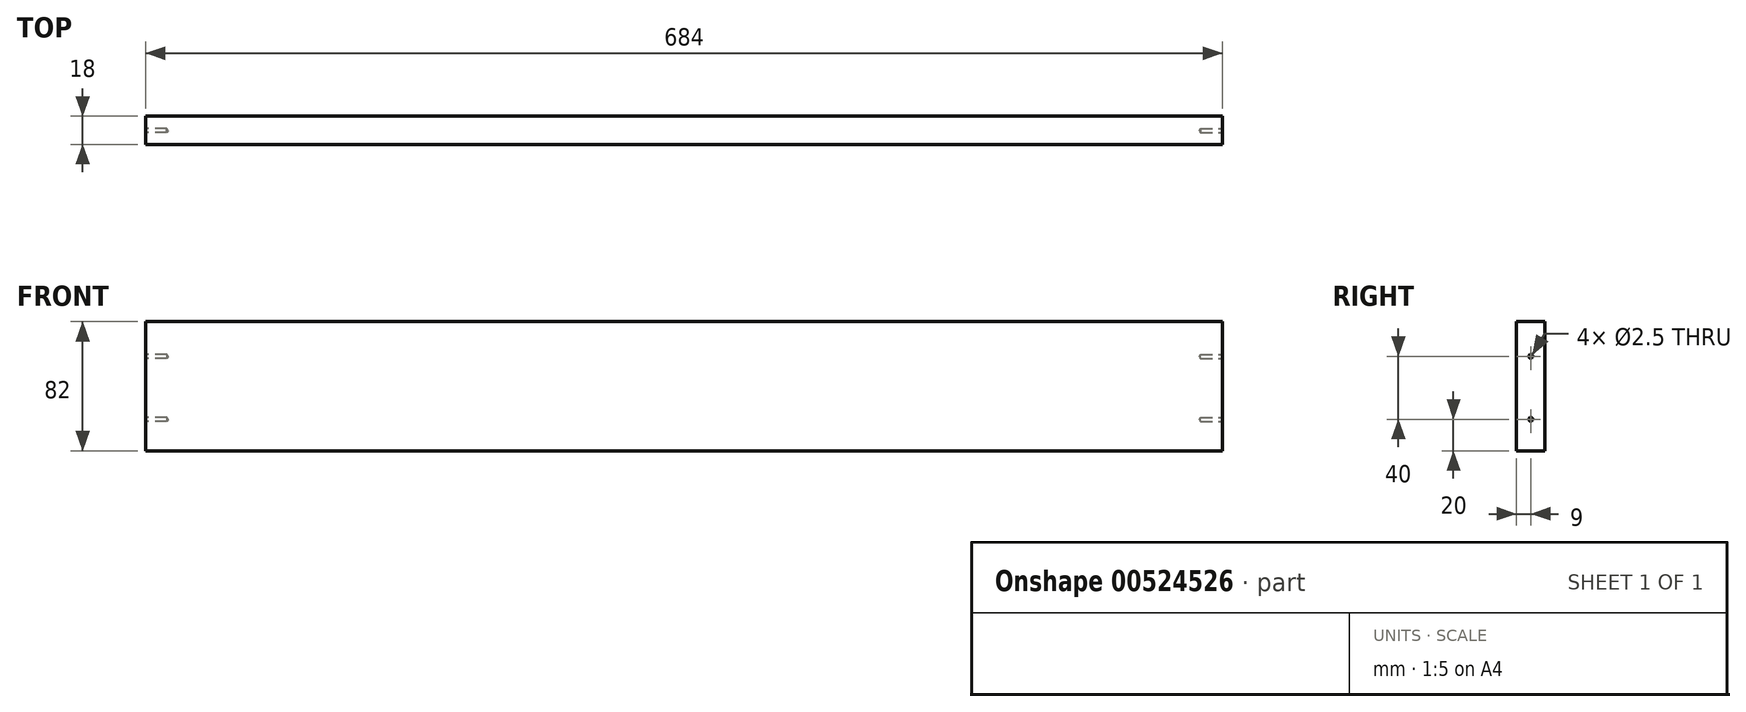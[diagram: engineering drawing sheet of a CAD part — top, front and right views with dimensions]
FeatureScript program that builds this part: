
annotation { "Feature Type Name" : "Feature", "Feature Type Description" : "" }
export const myFeature = defineFeature(function(context is Context, id is Id, definition is map)
    precondition{}
    {
        {
            var Q0;
            Q0=qCreatedBy(makeId("Front.planeOp"),FACE);
            var sketch = newSketch(context, id + "F0", { "sketchPlane" : qUnion([Q0])});
            skLineSegment(sketch, "E0.bottom", {"start": v(0, 0) * mm, "end": v(684, 0) * mm});
            skLineSegment(sketch, "E0.top", {"start": v(0, 82) * mm, "end": v(684, 82) * mm});
            skLineSegment(sketch, "E0.left", {"start": v(0, 0) * mm, "end": v(0, 82) * mm});
            skLineSegment(sketch, "E0.right", {"start": v(684, 0) * mm, "end": v(684, 82) * mm});
            skSolve(sketch);
        }
        {
            var Q0;
            Q0 = qSketchRegion(id + "F0", true);
            extrude(context, id + "F1", {"entities" : qUnion([Q0]), "depth" : 18 * mm, "offsetDistance" : 25 * mm});
        }
        {
            var Q0;
            Q0=makeQuery(id+"F1.opExtrude","SWEPT_FACE",FACE,{"disambiguationData":[OSD([sQuery(id+"F0.wireOp",EDGE,"E0.left")])]});
            var sketch = newSketch(context, id + "F2", { "sketchPlane" : qUnion([Q0])});
            skPoint(sketch, "E1", {"position": v(9, 20) * mm});
            skPoint(sketch, "E2", {"position": v(9, 60) * mm});
            skSolve(sketch);
        }
        {
            var Q0;
            Q0=sQuery(id+"F2.wireOp",VERTEX,"E1");
            var Q1;
            Q1=sQuery(id+"F2.wireOp",VERTEX,"E2");
            var Q2;
            Q2=makeQuery(id+"F1.opExtrude","SWEPT_BODY",BODY,{"disambiguationData":[OSD([sQuery(id+"F0.wireOp",EDGE,"E0.bottom"),sQuery(id+"F0.wireOp",EDGE,"E0.top"),sQuery(id+"F0.wireOp",EDGE,"E0.left"),sQuery(id+"F0.wireOp",EDGE,"E0.right")])]});
            hole(context, id + "F3", {"style" : HoleStyle.SIMPLE, "endStyle" : HoleEndStyle.BLIND, "standardTappedOrClearance" : lookupTablePath({ "standard" : "ISO", "engagement" : "75%", "pitch" : "0.5 mm", "size" : "M3", "type" : "Tapped" }), "standardBlindInLast" : lookupTablePath({ "standard" : "ISO", "engagement" : "75%", "pitch" : "0.5 mm", "size" : "M3", "type" : "Tapped" }), "holeDiameter" : 2.5 * mm, "showTappedDepth" : true, "holeDepth" : 13.5 * mm, "isTappedThrough" : true, "tappedDepth" : 12 * mm, "tapClearance" : 3, "locations" : qUnion([Q0, Q1]), "scope" : qUnion([Q2]), "majorDiameter" : 3 * mm});
        }
        {
            var Q0;
            Q0=makeQuery(id+"F1.opExtrude","SWEPT_FACE",FACE,{"disambiguationData":[OSD([sQuery(id+"F0.wireOp",EDGE,"E0.right")])]});
            var sketch = newSketch(context, id + "F4", { "sketchPlane" : qUnion([Q0])});
            skPoint(sketch, "E3", {"position": v(-9, 20) * mm});
            skPoint(sketch, "E4", {"position": v(-9, 60) * mm});
            skSolve(sketch);
        }
        {
            var Q0;
            Q0=sQuery(id+"F4.wireOp",VERTEX,"E3");
            var Q1;
            Q1=sQuery(id+"F4.wireOp",VERTEX,"E4");
            var Q2;
            Q2=makeQuery(id+"F1.opExtrude","SWEPT_BODY",BODY,{"disambiguationData":[OSD([sQuery(id+"F0.wireOp",EDGE,"E0.bottom"),sQuery(id+"F0.wireOp",EDGE,"E0.top"),sQuery(id+"F0.wireOp",EDGE,"E0.left"),sQuery(id+"F0.wireOp",EDGE,"E0.right")])]});
            hole(context, id + "F5", {"style" : HoleStyle.SIMPLE, "endStyle" : HoleEndStyle.BLIND, "standardTappedOrClearance" : lookupTablePath({ "standard" : "ISO", "engagement" : "75%", "pitch" : "0.5 mm", "size" : "M3", "type" : "Tapped" }), "standardBlindInLast" : lookupTablePath({ "standard" : "ISO", "engagement" : "75%", "pitch" : "0.5 mm", "size" : "M3", "type" : "Tapped" }), "holeDiameter" : 2.5 * mm, "showTappedDepth" : true, "holeDepth" : 14 * mm, "isTappedThrough" : true, "tappedDepth" : 12.5 * mm, "tapClearance" : 3, "locations" : qUnion([Q0, Q1]), "scope" : qUnion([Q2]), "majorDiameter" : 3 * mm});
        }
    });
